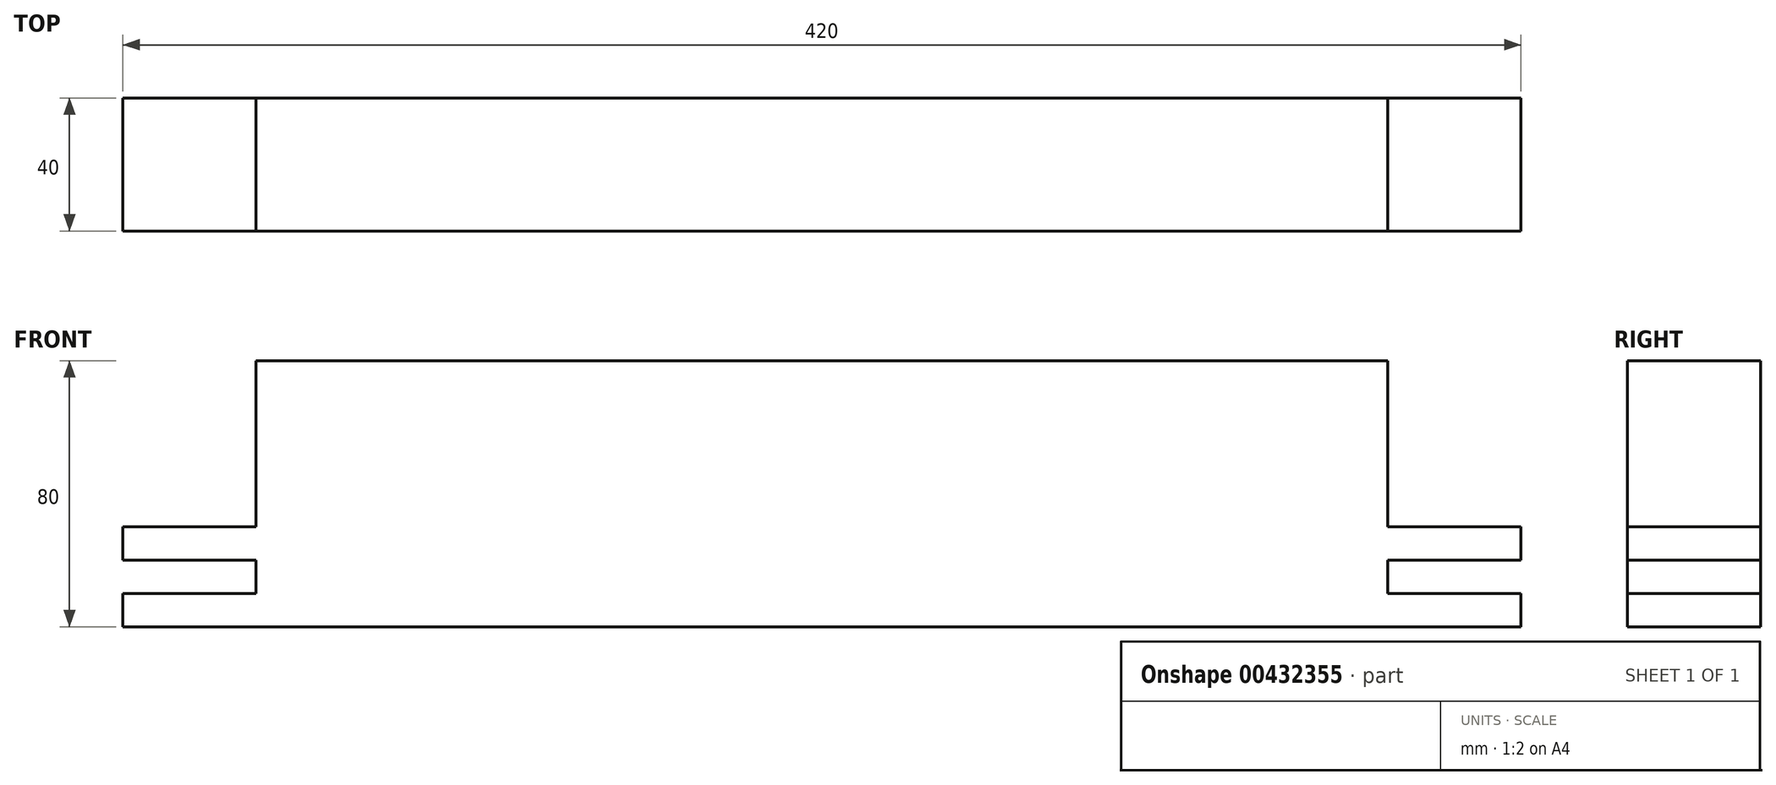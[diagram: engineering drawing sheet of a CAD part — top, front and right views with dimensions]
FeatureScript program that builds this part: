
annotation { "Feature Type Name" : "Feature", "Feature Type Description" : "" }
export const myFeature = defineFeature(function(context is Context, id is Id, definition is map)
    precondition{}
    {
        {
            var Q0;
            Q0=qCreatedBy(makeId("Front.planeOp"),FACE);
            var sketch = newSketch(context, id + "F0", { "sketchPlane" : qUnion([Q0])});
            skLineSegment(sketch, "E0.bottom", {"start": v(-170, 40) * mm, "end": v(170, 40) * mm});
            skLineSegment(sketch, "E0.top", {"start": v(-170, -40) * mm, "end": v(170, -40) * mm});
            skPoint(sketch, "E0.middle", {"position": v(0, 0) * mm});
            skLineSegment(sketch, "E1", {"start": v(-170, -40) * mm, "end": v(-210, -40) * mm});
            skLineSegment(sketch, "E2", {"start": v(-210, -40) * mm, "end": v(-210, -30) * mm});
            skLineSegment(sketch, "E3", {"start": v(-210, -30) * mm, "end": v(-170, -30) * mm});
            skLineSegment(sketch, "E4", {"start": v(-170, -30) * mm, "end": v(-170, -20) * mm});
            skLineSegment(sketch, "E5", {"start": v(-170, -20) * mm, "end": v(-210, -20) * mm});
            skLineSegment(sketch, "E6", {"start": v(-210, -20) * mm, "end": v(-210, -10) * mm});
            skLineSegment(sketch, "E7", {"start": v(-210, -10) * mm, "end": v(-170, -10) * mm});
            skLineSegment(sketch, "E8", {"start": v(-170, 40) * mm, "end": v(-170, -10) * mm});
            skLineSegment(sketch, "E9", {"start": v(170, -40) * mm, "end": v(210, -40) * mm});
            skLineSegment(sketch, "E10", {"start": v(210, -40) * mm, "end": v(210, -30) * mm});
            skLineSegment(sketch, "E11", {"start": v(210, -30) * mm, "end": v(170, -30) * mm});
            skLineSegment(sketch, "E12", {"start": v(170, -30) * mm, "end": v(170, -20) * mm});
            skLineSegment(sketch, "E13", {"start": v(170, -20) * mm, "end": v(210, -20) * mm});
            skLineSegment(sketch, "E14", {"start": v(210, -20) * mm, "end": v(210, -10) * mm});
            skLineSegment(sketch, "E15", {"start": v(210, -10) * mm, "end": v(170, -10) * mm});
            skLineSegment(sketch, "E16", {"start": v(170, 40) * mm, "end": v(170, -10) * mm});
            skSolve(sketch);
        }
        {
            var Q0;
            Q0=makeQuery(id+"F0.imprint","IMPRINT",FACE,{"disambiguationData":[TD([[makeQuery(id+"F0.imprint","IMPRINT",EDGE,{"derivedFrom":sQuery(id+"F0.wireOp",EDGE,"E0.bottom")}),-1.0]])]});
            extrude(context, id + "F1", {"entities" : qUnion([Q0]), "endBound" : BoundingType.SYMMETRIC, "depth" : 40 * mm});
        }
    });
